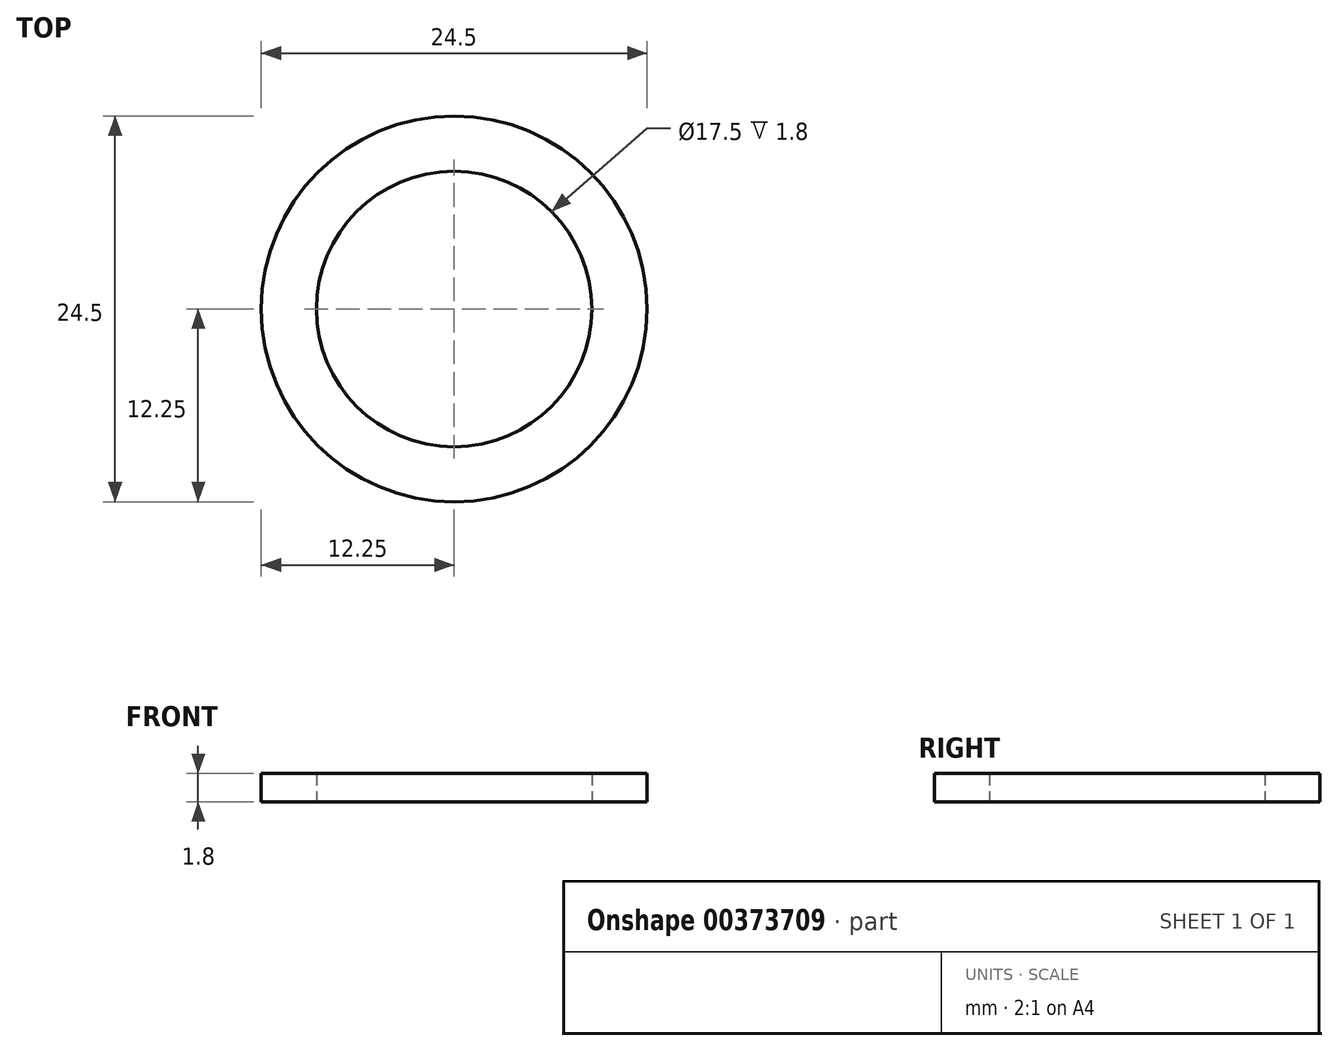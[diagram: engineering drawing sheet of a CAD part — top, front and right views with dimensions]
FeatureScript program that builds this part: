
annotation { "Feature Type Name" : "Feature", "Feature Type Description" : "" }
export const myFeature = defineFeature(function(context is Context, id is Id, definition is map)
    precondition{}
    {
        {
            var Q0;
            Q0=qCreatedBy(makeId("Top.planeOp"),FACE);
            var sketch = newSketch(context, id + "F0", { "sketchPlane" : qUnion([Q0])});
            skCircle(sketch, "E0", {"center": v(0, 0) * mm, "radius": 8.75 * mm});
            skCircle(sketch, "E1", {"center": v(0, 0) * mm, "radius": 12.25 * mm});
            skSolve(sketch);
        }
        {
            var Q0;
            Q0=makeQuery(id+"F0.imprint","IMPRINT",FACE,{"disambiguationData":[TD([[makeQuery(id+"F0.imprint","IMPRINT",EDGE,{"derivedFrom":sQuery(id+"F0.wireOp",EDGE,"E0")}),-1.0]])]});
            extrude(context, id + "F1", {"entities" : qUnion([Q0]), "depth" : 1.8 * mm});
        }
    });
